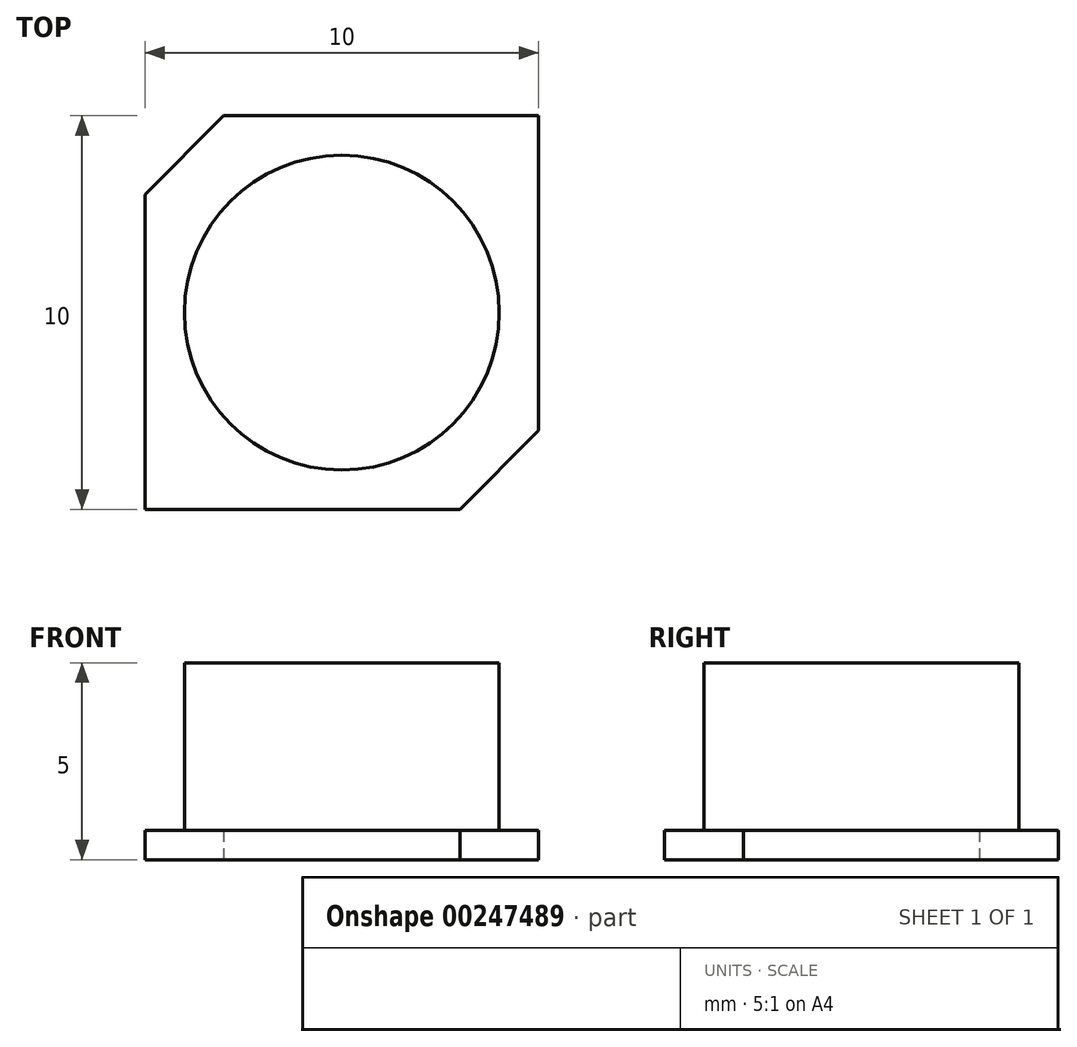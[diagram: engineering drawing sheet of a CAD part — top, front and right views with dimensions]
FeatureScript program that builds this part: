
annotation { "Feature Type Name" : "Feature", "Feature Type Description" : "" }
export const myFeature = defineFeature(function(context is Context, id is Id, definition is map)
    precondition{}
    {
        {
            var Q0;
            Q0=qCreatedBy(makeId("Top.planeOp"),FACE);
            var sketch = newSketch(context, id + "F0", { "sketchPlane" : qUnion([Q0])});
            skLineSegment(sketch, "E0.rect.bottom", {"start": v(3, -5) * mm, "end": v(-5, -5) * mm});
            skLineSegment(sketch, "E0.rect.top", {"start": v(5, 5) * mm, "end": v(-3, 5) * mm});
            skLineSegment(sketch, "E0.rect.left", {"start": v(5, -3) * mm, "end": v(5, 5) * mm});
            skLineSegment(sketch, "E0.rect.right", {"start": v(-5, -5) * mm, "end": v(-5, 3) * mm});
            skPoint(sketch, "E0.rect.middle", {"position": v(0, 0) * mm});
            skLineSegment(sketch, "E1", {"start": v(-5, 3) * mm, "end": v(-3, 5) * mm});
            skLineSegment(sketch, "E2", {"start": v(5, -3) * mm, "end": v(3, -5) * mm});
            skPoint(sketch, "E3.orphan", {"position": v(-5, 5) * mm});
            skPoint(sketch, "E4.orphan", {"position": v(5, -5) * mm});
            skSolve(sketch);
        }
        {
            var Q0;
            Q0=makeQuery(id+"F0.imprint","IMPRINT",FACE,{"disambiguationData":[TD([[makeQuery(id+"F0.imprint","IMPRINT",EDGE,{"derivedFrom":sQuery(id+"F0.wireOp",EDGE,"E0.rect.bottom")}),-1.0]])]});
            extrude(context, id + "F1", {"entities" : qUnion([Q0]), "depth" : 0.75 * mm});
        }
        {
            var Q0;
            Q0=qCreatedBy(makeId("Top.planeOp"),FACE);
            var sketch = newSketch(context, id + "F2", { "sketchPlane" : qUnion([Q0])});
            skCircle(sketch, "E5", {"center": v(0, 0) * mm, "radius": 4 * mm});
            skSolve(sketch);
        }
        {
            var Q0;
            Q0=qSketchRegion(id+"F2",true);
            extrude(context, id + "F3", {"entities" : qUnion([Q0]), "operationType" : NewBodyOperationType.ADD, "depth" : 5 * mm});
        }
    });
